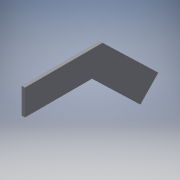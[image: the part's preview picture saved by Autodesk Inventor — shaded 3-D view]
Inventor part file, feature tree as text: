
AUTODESK INVENTOR PART (.ipt)
format: ipt  version: 2016 (Build 200138000, 138)  size: 94,208 bytes
history: native  units: in
note: dims shown in document units (in); Inventor stores cm internally (conversion verified against a paired STEP export)
features: extrude x1, sketch x1
ambient origin geometry x8: Origin, YZ Plane, XZ Plane, XY Plane, X Axis, Y Axis, Z Axis, Center Point
bodies: Solid1 (feature_tree)
feature tree (2):
  extrude  "Extrusion1"  Depth=1.0in
  sketch  "Sketch1"  dims[d0=4.0in d1=1.0in d2=1.0in d3=3.0in d4=0.9351in d5=0.125in d6=0.0in]
